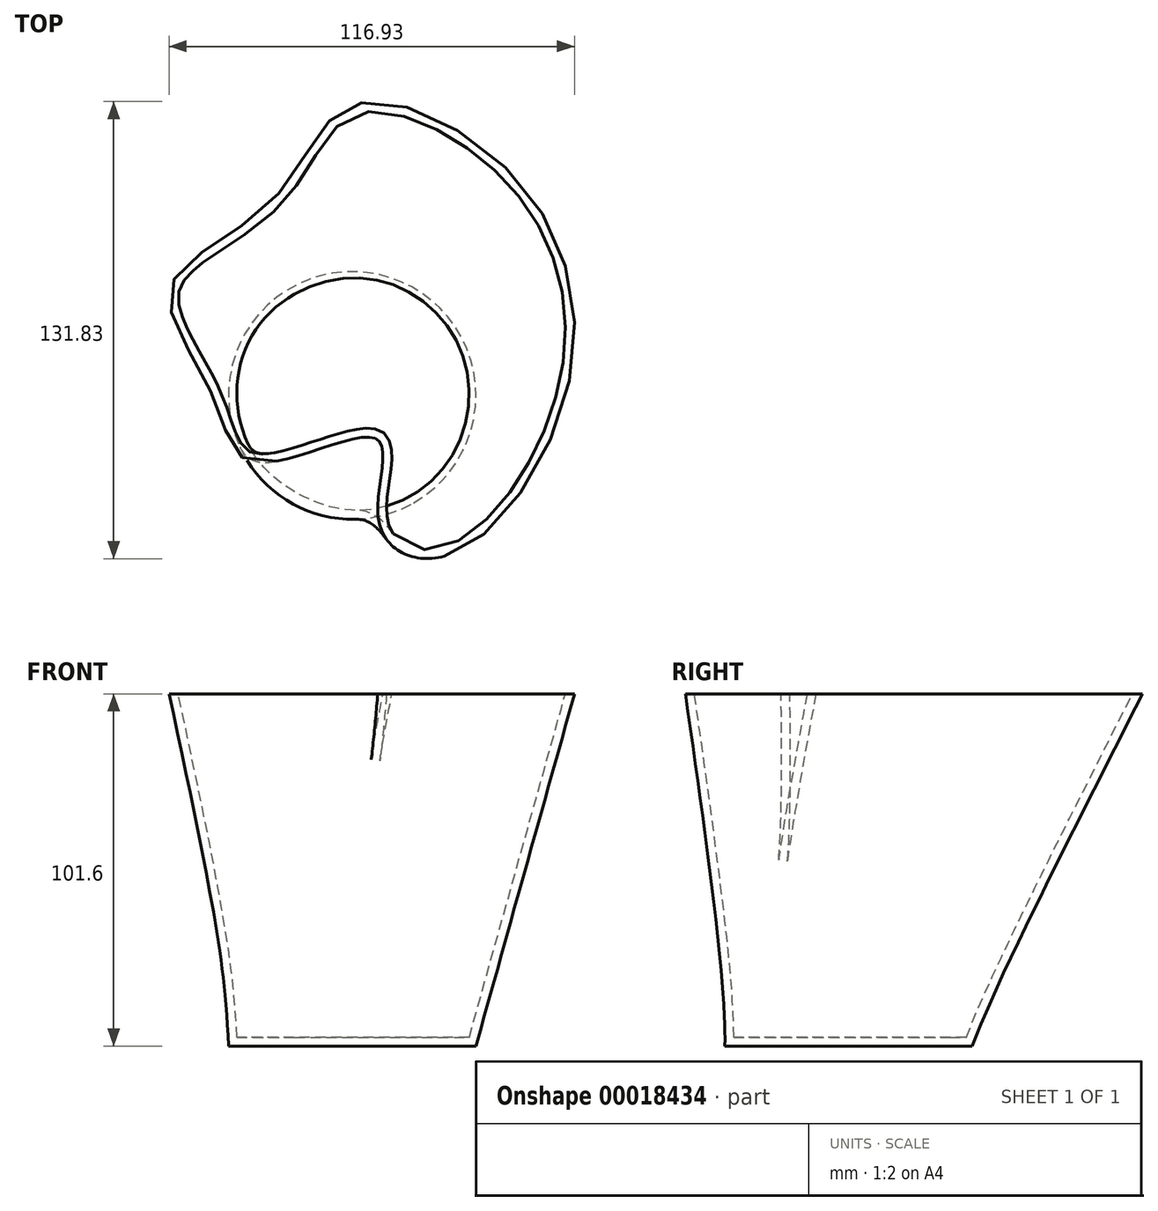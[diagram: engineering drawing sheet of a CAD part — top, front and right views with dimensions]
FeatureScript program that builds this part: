
annotation { "Feature Type Name" : "Feature", "Feature Type Description" : "" }
export const myFeature = defineFeature(function(context is Context, id is Id, definition is map)
    precondition{}
    {
        {
            var Q0;
            Q0=qCreatedBy(makeId("Top.planeOp"),FACE);
            cPlane(context, id + "F0", {"entities" : qUnion([Q0]), "cplaneType" : CPlaneType.OFFSET, "offset" : 101.6 * mm, "width" : 152.4 * mm, "height" : 152.4 * mm});
        }
        {
            var Q0;
            Q0=qCreatedBy(makeId("Top.planeOp"),FACE);
            var sketch = newSketch(context, id + "F1", { "sketchPlane" : qUnion([Q0])});
            skCircle(sketch, "E0", {"center": v(0, 0) * mm, "radius": 35.69 * mm});
            skSolve(sketch);
        }
        {
            var Q0;
            Q0=qCreatedBy(id+"F0.planeOp",FACE);
            var sketch = newSketch(context, id + "F2", { "sketchPlane" : qUnion([Q0])});
            skFitSpline(sketch, "E1", {"points": [v(26.53, -46.44) * mm, v(7.75, -36.8) * mm, v(7.16, -12.69) * mm, v(-27.93, -19.4) * mm, v(-40.3, 0) * mm, v(-52.4, 31.21) * mm, v(-23.06, 56.2) * mm, v(0, 83.78) * mm, v(48.34, 61.44) * mm, v(61.61, 0) * mm, v(26.53, -46.44) * mm]});
            skSolve(sketch);
        }
        {
            var Q0;
            Q0=makeQuery(id+"F2.imprint","IMPRINT",FACE,{"disambiguationData":[TD([[makeQuery(id+"F2.imprint","IMPRINT",EDGE,{"derivedFrom":sQuery(id+"F2.wireOp",EDGE,"E1")}),-1.0]])]});
            var Q1;
            Q1=makeQuery(id+"F1.imprint","IMPRINT",FACE,{"disambiguationData":[TD([[makeQuery(id+"F1.imprint","IMPRINT",EDGE,{"derivedFrom":sQuery(id+"F1.wireOp",EDGE,"E0")}),1.0]])]});
            loft(context, id + "F3", {"sheetProfilesArray" : [{ "sheetProfileEntities" : qUnion([Q0]) }, { "sheetProfileEntities" : qUnion([Q1]) }]});
        }
        {
            var Q0;
            Q0=makeQuery(id+"F3.opLoft","CAP_FACE",FACE,{"disambiguationData":[OSD([makeQuery(id+"F2.imprint","IMPRINT",FACE,{"disambiguationData":[TD([[makeQuery(id+"F2.imprint","IMPRINT",EDGE,{"derivedFrom":sQuery(id+"F2.wireOp",EDGE,"E1")}),-1.0]])]})])],"isStart":true});
            shell(context, id + "F4", {"entities" : qUnion([Q0]), "thickness" : 2.54 * mm});
        }
        {
            var Q0;
            Q0=qCreatedBy(makeId("Front.planeOp"),FACE);
            var sketch = newSketch(context, id + "F5", { "sketchPlane" : qUnion([Q0])});
            skFitSpline(sketch, "E2", {"points": [v(63.66, 100.49) * mm, v(89.81, 98.71) * mm, v(100.95, 88.46) * mm, v(108.58, 67.23) * mm, v(95.25, 55.94) * mm, v(102.4, 44.33) * mm, v(87.83, 30.86) * mm, v(89.23, 14.53) * mm, v(63.76, 6.68) * mm, v(35.9, 0) * mm], "startDerivative": vector(236.98, 6.7) * mm, "endDerivative": vector(-192.32, -57.05) * mm});
            skSolve(sketch);
        }
    });
